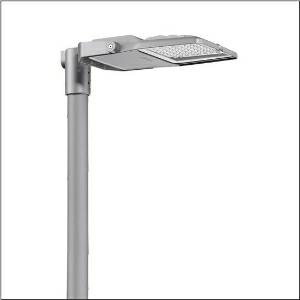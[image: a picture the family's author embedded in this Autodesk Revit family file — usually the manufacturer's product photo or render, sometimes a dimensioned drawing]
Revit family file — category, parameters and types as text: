
# Revit family: floodlight_fl_21_mini___pl33t_5xa7771c2f3a_f864
name_source: partatom
category: Lighting Fixtures
units: mm (PartAtom-declared; Revit-internal decimal feet)

## family parameters
Cut with Voids When Loaded = No
Host = Face
Light Source = No
Part Type = Normal
Room Calculation Point = No
Round Connector Dimension = Use Diameter
Shared = No

## types (1)
- --- (1 x LED, 12060 lm, 87.2 W, 3000K)
    Apparent Load = 87 VA
    CIE Flux Codes = 26 75 99 100 100
    Color Rendering = 70
    Color Temperature = 3000K
    Default Elevation = 1800 mm
    Description = Floodlight FL 21 mini, floodlight, primary light control with lens, of PMMA, primary optical cover: protective disc, of toughened safety glass, transparent, light distribution: PL33T, light emission: direct distribution, installation type: surface-mounted, LED, High Power LED, rated luminous flux: 12.060lm, luminous efficacy: 138lm/W, light colour: 730, colour temperature: 3000K, control gear: ECG iQ, control: Auto-Match, Temp-Guard, Lumen-Switch, Night-Set, Smart-Wire, Light-Fading, Desk-Remote (wireless, voltage-free reading and setting of iQ features in the workshop via application-optimized NFC function/RFID function), optimised constant luminous flux control (CLO 2.0), with terminal, 6-pole, mains connection: 220..240V, AC, 50/60Hz, start of lifetime: 87W, end of lifetime: 92W, reduction: 40W, luminaire housing, of diecast aluminium, powder-coated, Siteco® metallic grey (DB 702S), corrosivity category C5 according to DIN EN ISO 12944, mast bracket, of steel, galvanised, powder-coated, Siteco® metallic grey (DB 702S), protection rating (complete): IP66, insulation class (complete): insulation class II (safety insulation), certification: CE, ENEC, VDE, protection symbol: D, impact resistance: IK08, permissible operating ambient temperature: -40..+40°C, permissible operating ambient temperature for outdoor applications: -40..+50°C, standard: DIN EN 12944, packaging unit: 1 piece

Light Distribution: PL33T
    Height = 70 mm
    Lamp = 1 x LED
    Lamp Light Flux = 12060 lm
    Lamp Power = 87.2 W
    Lamp count = 1
    Length = 485 mm
    Luminous efficacy = 138 lm/W
    Manufacturer = Siteco
    ModVariant = No
    Model = 5XA7771C2F3A
    Number of Poles = 1
    OnlyDefault = Yes
    Power Factor = 1
    Product Name = Floodlight FL 21 mini | PL33T
    Product group = floodlight | pylon top
    ProductGroupID = 6101
    Protection Class = Protection class II
    Protection Degree = IP 66
    RLX_Detail_Level = 1
    RlxData = <blob elided: 101077 chars, md5=1f19f930>
    Socket = socket
    Standby Power = 0 W
    System Light Flux = 12060 lm
    System Power = 87 W
    Type Comments = factory setting: luminous flux: 100 % | dim-lin: 254 | 456 mA
    Type Image = l_1007125.jpg
    URL = http://relux.com
    VarID = @adj_059765
    Voltage = 0 V
    Weight = 0.00 kg
    Width = 337 mm

## geometry (parser evidence)
native form markers: Blend x4, Sweep x10
no freeform markers — native parametric forms only
